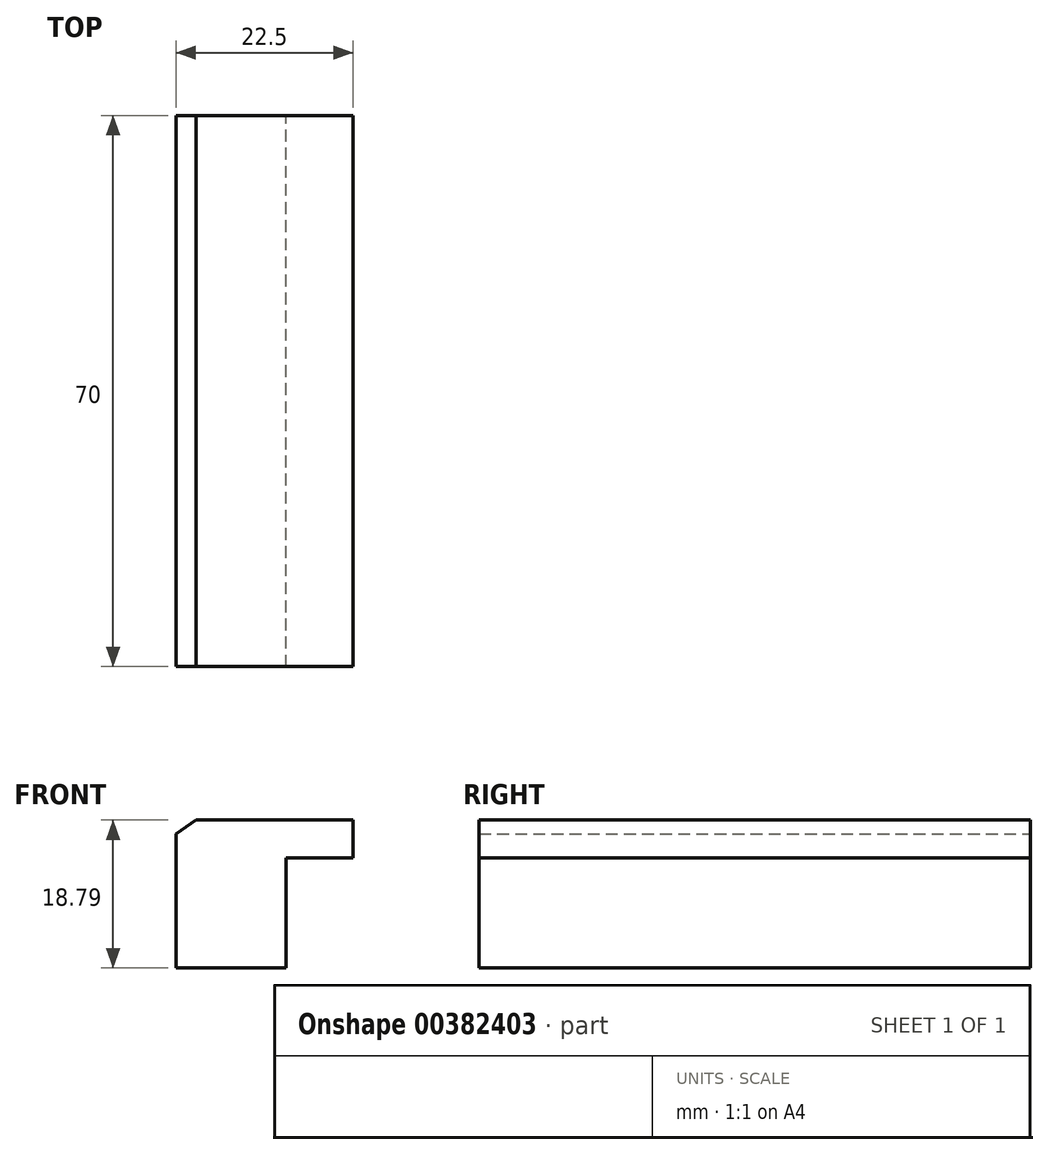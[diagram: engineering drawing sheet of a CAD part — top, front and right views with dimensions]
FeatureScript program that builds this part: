
annotation { "Feature Type Name" : "Feature", "Feature Type Description" : "" }
export const myFeature = defineFeature(function(context is Context, id is Id, definition is map)
    precondition{}
    {
        {
            var Q0;
            Q0=qCreatedBy(makeId("Front.planeOp"),FACE);
            var sketch = newSketch(context, id + "F0", { "sketchPlane" : qUnion([Q0])});
            skLineSegment(sketch, "E0", {"start": v(-9.2, 0) * mm, "end": v(-9.2, -17) * mm});
            skLineSegment(sketch, "E1", {"start": v(-9.2, -17) * mm, "end": v(4.8, -17) * mm});
            skLineSegment(sketch, "E2", {"start": v(4.8, -17) * mm, "end": v(4.8, -3) * mm});
            skLineSegment(sketch, "E3", {"start": v(-9.2, 0) * mm, "end": v(-6.64, 1.8) * mm});
            skLineSegment(sketch, "E4", {"start": v(-6.64, 1.8) * mm, "end": v(13.3, 1.8) * mm});
            skLineSegment(sketch, "E5", {"start": v(4.8, -3) * mm, "end": v(13.3, -3) * mm});
            skLineSegment(sketch, "E6", {"start": v(13.3, -3) * mm, "end": v(13.3, 1.8) * mm});
            skSolve(sketch);
        }
        {
            var Q0;
            Q0=makeQuery(id+"F0.imprint","IMPRINT",FACE,{"disambiguationData":[TD([[makeQuery(id+"F0.imprint","IMPRINT",EDGE,{"derivedFrom":sQuery(id+"F0.wireOp",EDGE,"E0")}),1.0]])]});
            extrude(context, id + "F1", {"entities" : qUnion([Q0]), "depth" : 70 * mm});
        }
    });
